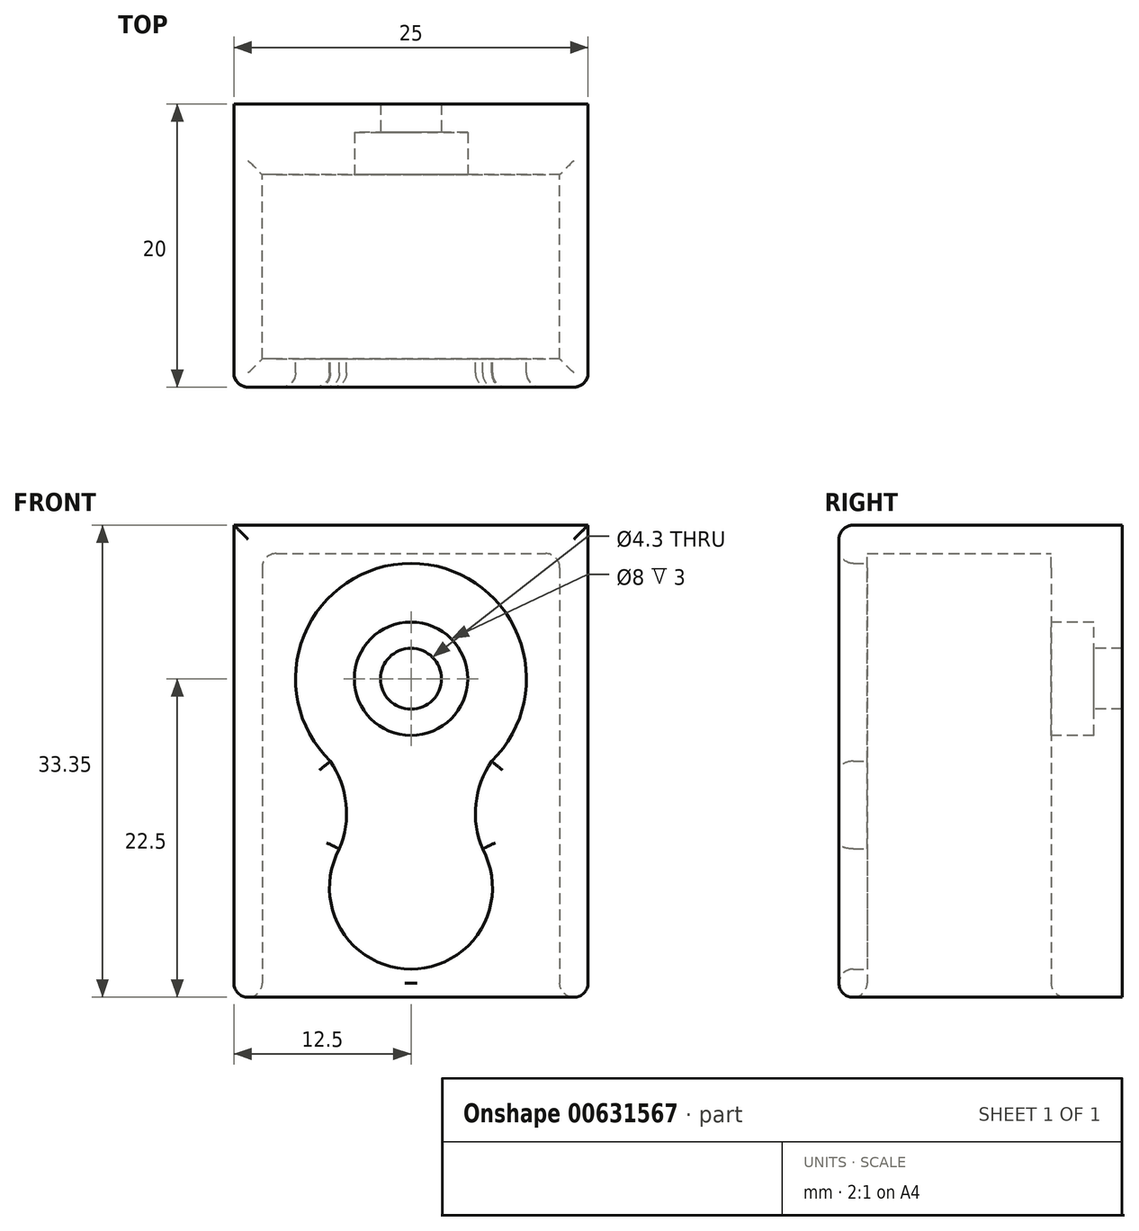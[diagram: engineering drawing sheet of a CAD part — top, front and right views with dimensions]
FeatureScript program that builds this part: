
annotation { "Feature Type Name" : "Feature", "Feature Type Description" : "" }
export const myFeature = defineFeature(function(context is Context, id is Id, definition is map)
    precondition{}
    {
        {
            var Q0;
            Q0=qCreatedBy(makeId("Front.planeOp"),FACE);
            var sketch = newSketch(context, id + "F0", { "sketchPlane" : qUnion([Q0])});
            skLineSegment(sketch, "E0.bottom", {"start": v(12.5, -22.5) * mm, "end": v(-12.5, -22.5) * mm});
            skLineSegment(sketch, "E0.top", {"start": v(12.5, 22.5) * mm, "end": v(-12.5, 22.5) * mm});
            skLineSegment(sketch, "E0.left", {"start": v(12.5, -22.5) * mm, "end": v(12.5, 22.5) * mm});
            skLineSegment(sketch, "E0.right", {"start": v(-12.5, -22.5) * mm, "end": v(-12.5, 22.5) * mm});
            skPoint(sketch, "E0.middle", {"position": v(0, 0) * mm});
            skCircle(sketch, "E1", {"center": v(0, 17.3) * mm, "radius": 2.15 * mm});
            skSolve(sketch);
        }
        {
            var Q0;
            Q0=makeQuery(id+"F0.imprint","IMPRINT",FACE,{"disambiguationData":[TD([[makeQuery(id+"F0.imprint","IMPRINT",EDGE,{"derivedFrom":sQuery(id+"F0.wireOp",EDGE,"E0.bottom")}),-1.0]])]});
            extrude(context, id + "F1", {"entities" : qUnion([Q0]), "depth" : 5 * mm, "offsetDistance" : 25 * mm});
        }
        {
            var Q0;
            Q0=makeQuery(id+"F1.opExtrude","CAP_FACE",FACE,{"disambiguationData":[OSD([sQuery(id+"F0.wireOp",EDGE,"E0.bottom"),sQuery(id+"F0.wireOp",EDGE,"E0.top"),sQuery(id+"F0.wireOp",EDGE,"E0.left"),sQuery(id+"F0.wireOp",EDGE,"E0.right"),sQuery(id+"F0.wireOp",EDGE,"E1")])],"isStart":false});
            var sketch = newSketch(context, id + "F2", { "sketchPlane" : qUnion([Q0])});
            skCircle(sketch, "E2", {"center": v(0, 17.3) * mm, "radius": 4 * mm});
            skSolve(sketch);
        }
        {
            var Q0;
            Q0 = qSketchRegion(id + "F2", true);
            extrude(context, id + "F3", {"entities" : qUnion([Q0]), "operationType" : NewBodyOperationType.REMOVE, "oppositeDirection" : true, "depth" : 3 * mm, "offsetDistance" : 25 * mm});
        }
        {
            var Q0;
            Q0=makeQuery(id+"F1.opExtrude","CAP_FACE",FACE,{"disambiguationData":[OSD([sQuery(id+"F0.wireOp",EDGE,"E0.bottom"),sQuery(id+"F0.wireOp",EDGE,"E0.top"),sQuery(id+"F0.wireOp",EDGE,"E0.left"),sQuery(id+"F0.wireOp",EDGE,"E0.right"),sQuery(id+"F0.wireOp",EDGE,"E1")])],"isStart":false});
            var sketch = newSketch(context, id + "F4", { "sketchPlane" : qUnion([Q0])});
            skLineSegment(sketch, "E3.bottom", {"start": v(-12.5, 10.85) * mm, "end": v(12.5, 10.85) * mm});
            skLineSegment(sketch, "E3.top", {"start": v(-12.5, -22.5) * mm, "end": v(-10.5, -22.5) * mm});
            skLineSegment(sketch, "E3.left", {"start": v(-12.5, 10.85) * mm, "end": v(-12.5, -22.5) * mm});
            skLineSegment(sketch, "E3.right", {"start": v(12.5, 10.85) * mm, "end": v(12.5, -22.5) * mm});
            skLineSegment(sketch, "E4.0", {"start": v(-10.5, 8.85) * mm, "end": v(10.5, 8.85) * mm});
            skLineSegment(sketch, "E4.1", {"start": v(-10.5, 8.85) * mm, "end": v(-10.5, -20.5) * mm});
            skLineSegment(sketch, "E4.3", {"start": v(10.5, 8.85) * mm, "end": v(10.5, -20.5) * mm});
            skLineSegment(sketch, "E5", {"start": v(10.5, -20.5) * mm, "end": v(10.5, -22.5) * mm});
            skLineSegment(sketch, "E6", {"start": v(-10.5, -20.5) * mm, "end": v(-10.5, -22.5) * mm});
            skLineSegment(sketch, "E7.trimOffspring", {"start": v(10.5, -22.5) * mm, "end": v(12.5, -22.5) * mm});
            skSolve(sketch);
        }
        {
            var Q0;
            Q0 = qSketchRegion(id + "F4", true);
            extrude(context, id + "F5", {"entities" : qUnion([Q0]), "operationType" : NewBodyOperationType.ADD, "depth" : 13 * mm, "offsetDistance" : 25 * mm});
        }
        {
            var Q0;
            Q0=makeQuery(id+"F5.opExtrude","CAP_FACE",FACE,{"disambiguationData":[OSD([sQuery(id+"F4.wireOp",EDGE,"E3.bottom"),sQuery(id+"F4.wireOp",EDGE,"E3.top"),sQuery(id+"F4.wireOp",EDGE,"E3.left"),sQuery(id+"F4.wireOp",EDGE,"E3.right"),sQuery(id+"F4.wireOp",EDGE,"E4.0"),sQuery(id+"F4.wireOp",EDGE,"E4.1"),sQuery(id+"F4.wireOp",EDGE,"E4.3"),sQuery(id+"F4.wireOp",EDGE,"E5"),sQuery(id+"F4.wireOp",EDGE,"E6"),sQuery(id+"F4.wireOp",EDGE,"E7.trimOffspring")])],"isStart":false});
            var sketch = newSketch(context, id + "F6", { "sketchPlane" : qUnion([Q0])});
            skLineSegment(sketch, "E8.0", {"start": v(-12.5, 10.85) * mm, "end": v(12.5, 10.85) * mm});
            skLineSegment(sketch, "E8.1", {"start": v(-12.5, -22.5) * mm, "end": v(-12.5, 10.85) * mm});
            skLineSegment(sketch, "E8.2", {"start": v(12.5, -22.5) * mm, "end": v(12.5, 10.85) * mm});
            skLineSegment(sketch, "E9", {"start": v(12.5, -22.5) * mm, "end": v(-12.5, -22.5) * mm});
            skArc(sketch, "E10", {"start": v(5.7, -5.83) * mm, "mid": v(0, 8.15) * mm, "end": v(-5.7, -5.83) * mm});
            skArc(sketch, "E11", {"start": v(-5.05, -12.02) * mm, "mid": v(0, -20.51) * mm, "end": v(5.05, -12.02) * mm});
            skArc(sketch, "E12", {"start": v(-5.32, -12.58) * mm, "mid": v(-4.56, -9.15) * mm, "end": v(-5.7, -5.83) * mm});
            skPoint(sketch, "E12.endSnap0", {"position": v(-12.5, -5.83) * mm});
            skLineSegment(sketch, "E13", {"start": v(0, 8.85) * mm, "end": v(0, -22.5) * mm, "construction": true});
            skArc(sketch, "E14.MirrorCS", {"start": v(5.32, -12.58) * mm, "mid": v(4.56, -9.15) * mm, "end": v(5.7, -5.83) * mm});
            skSolve(sketch);
        }
        {
            var Q0;
            {var subQ4=sQuery(id+"F6.wireOp",EDGE,"E10");Q0=makeQuery(id+"F6.imprint","IMPRINT",FACE,{"disambiguationData":[TD([[makeQuery(id+"F6.imprint","IMPRINT",EDGE,{"derivedFrom":subQ4}),-1.0]])]});}
            var Q1;
            Q1=makeQuery(id+"F6.imprint","IMPRINT",FACE,{"disambiguationData":[TD([[makeQuery(id+"F6.imprint","IMPRINT",EDGE,{"derivedFrom":sQuery(id+"F6.wireOp",EDGE,"E8.0")}),-1.0]])]});
            extrude(context, id + "F7", {"entities" : qUnion([Q0, Q1]), "operationType" : NewBodyOperationType.ADD, "depth" : 2 * mm, "offsetDistance" : 25 * mm});
        }
        {
            var Q0;
            {var subQ0=sQuery(id+"F0.wireOp",EDGE,"E0.right");var subQ1=sQuery(id+"F0.wireOp",EDGE,"E0.left");var subQ2=sQuery(id+"F0.wireOp",EDGE,"E0.top");Q0=makeQuery(id+"F5.boolean.opBoolean","SPLIT",FACE,{"disambiguationData":[TD([makeQuery(id+"F1.opExtrude","SWEPT_FACE",FACE,{"disambiguationData":[OSD([subQ2])]})])],"derivedFrom":makeQuery(id+"F1.opExtrude","CAP_FACE",FACE,{"disambiguationData":[OSD([sQuery(id+"F0.wireOp",EDGE,"E0.bottom"),subQ2,subQ1,subQ0,sQuery(id+"F0.wireOp",EDGE,"E1")])],"isStart":false})});}
            var sketch = newSketch(context, id + "F8", { "sketchPlane" : qUnion([Q0])});
            skLineSegment(sketch, "E15.0", {"start": v(12.5, 22.5) * mm, "end": v(-12.5, 22.5) * mm});
            skLineSegment(sketch, "E15.1", {"start": v(-12.5, 10.85) * mm, "end": v(-12.5, 22.5) * mm});
            skLineSegment(sketch, "E15.2", {"start": v(-12.5, 10.85) * mm, "end": v(12.5, 10.85) * mm});
            skLineSegment(sketch, "E15.3", {"start": v(12.5, 10.85) * mm, "end": v(12.5, 22.5) * mm});
            skSolve(sketch);
        }
        {
            var Q0;
            Q0 = qSketchRegion(id + "F8", true);
            var Q1;
            Q1=makeQuery(id+"F1.opExtrude","CAP_FACE",FACE,{"disambiguationData":[OSD([sQuery(id+"F0.wireOp",EDGE,"E0.bottom"),sQuery(id+"F0.wireOp",EDGE,"E0.top"),sQuery(id+"F0.wireOp",EDGE,"E0.left"),sQuery(id+"F0.wireOp",EDGE,"E0.right"),sQuery(id+"F0.wireOp",EDGE,"E1")])],"isStart":true});
            extrude(context, id + "F9", {"entities" : qUnion([Q0]), "operationType" : NewBodyOperationType.REMOVE, "endBound" : BoundingType.UP_TO_SURFACE, "oppositeDirection" : true, "depth" : 25 * mm, "endBoundEntityFace" : qUnion([Q1]), "offsetDistance" : 25 * mm});
        }
        {
            var Q0;
            {var subQ0=sQuery(id+"F0.wireOp",EDGE,"E0.bottom");Q0=makeQuery(id+"F5.boolean.opBoolean","SPLIT",FACE,{"disambiguationData":[TD([makeQuery(id+"F1.opExtrude","SWEPT_FACE",FACE,{"disambiguationData":[OSD([subQ0])]})])],"derivedFrom":makeQuery(id+"F1.opExtrude","CAP_FACE",FACE,{"disambiguationData":[OSD([subQ0,sQuery(id+"F0.wireOp",EDGE,"E0.top"),sQuery(id+"F0.wireOp",EDGE,"E0.left"),sQuery(id+"F0.wireOp",EDGE,"E0.right"),sQuery(id+"F0.wireOp",EDGE,"E1")])],"isStart":false})});}
            var sketch = newSketch(context, id + "F10", { "sketchPlane" : qUnion([Q0])});
            skCircle(sketch, "E16", {"center": v(0, 0) * mm, "radius": 2.15 * mm});
            skSolve(sketch);
        }
        {
            var Q0;
            Q0=makeQuery(id+"F10.imprint","IMPRINT",FACE,{"disambiguationData":[TD([[makeQuery(id+"F10.imprint","IMPRINT",EDGE,{"derivedFrom":sQuery(id+"F10.wireOp",EDGE,"E16")}),1.0]])]});
            extrude(context, id + "F11", {"entities" : qUnion([Q0]), "operationType" : NewBodyOperationType.REMOVE, "endBound" : BoundingType.UP_TO_NEXT, "oppositeDirection" : true, "depth" : 25 * mm, "offsetDistance" : 25 * mm});
        }
        {
            var Q0;
            {var subQ0=sQuery(id+"F0.wireOp",EDGE,"E0.bottom");Q0=makeQuery(id+"F5.boolean.opBoolean","SPLIT",FACE,{"disambiguationData":[TD([makeQuery(id+"F1.opExtrude","SWEPT_FACE",FACE,{"disambiguationData":[OSD([subQ0])]})])],"derivedFrom":makeQuery(id+"F1.opExtrude","CAP_FACE",FACE,{"disambiguationData":[OSD([subQ0,sQuery(id+"F0.wireOp",EDGE,"E0.top"),sQuery(id+"F0.wireOp",EDGE,"E0.left"),sQuery(id+"F0.wireOp",EDGE,"E0.right"),sQuery(id+"F0.wireOp",EDGE,"E1")])],"isStart":false})});}
            var sketch = newSketch(context, id + "F12", { "sketchPlane" : qUnion([Q0])});
            skCircle(sketch, "E17", {"center": v(0, 0) * mm, "radius": 4 * mm});
            skSolve(sketch);
        }
        {
            var Q0;
            Q0 = qSketchRegion(id + "F12", true);
            extrude(context, id + "F13", {"entities" : qUnion([Q0]), "operationType" : NewBodyOperationType.REMOVE, "oppositeDirection" : true, "depth" : 3 * mm, "offsetDistance" : 25 * mm});
        }
        {
            var Q0;
            Q0=makeQuery(id+"F7.opExtrude","CAP_EDGE",EDGE,{"disambiguationData":[OSD([sQuery(id+"F6.wireOp",EDGE,"E8.0")])],"isStart":false});
            var Q1;
            Q1=makeQuery(id+"F7.opExtrude","CAP_EDGE",EDGE,{"disambiguationData":[OSD([sQuery(id+"F6.wireOp",EDGE,"E8.1")])],"isStart":false});
            var Q2;
            Q2=makeQuery(id+"F7.opExtrude","CAP_EDGE",EDGE,{"disambiguationData":[OSD([sQuery(id+"F6.wireOp",EDGE,"E8.2")])],"isStart":false});
            var Q3;
            Q3=makeQuery(id+"F7.opExtrude","CAP_EDGE",EDGE,{"disambiguationData":[OSD([sQuery(id+"F6.wireOp",EDGE,"E9")])],"isStart":false});
            var Q4;
            Q4=makeQuery(id+"F9.boolean.opBoolean","MERGE",EDGE,{"derivedFrom":[makeQuery(id+"F7.boolean.opBoolean","MERGE",EDGE,{"derivedFrom":[makeQuery(id+"F5.opExtrude","SWEPT_EDGE",EDGE,{"disambiguationData":[OSD([sQuery(id+"F0.wireOp",EDGE,"E0.left"),sQuery(id+"F4.wireOp",EDGE,"E3.bottom"),sQuery(id+"F4.wireOp",EDGE,"E3.right")])]}),makeQuery(id+"F7.opExtrude","SWEPT_EDGE",EDGE,{"disambiguationData":[OSD([sQuery(id+"F6.wireOp",EDGE,"E8.0"),sQuery(id+"F6.wireOp",EDGE,"E8.2")])]})]}),makeQuery(id+"F9.opExtrude","SWEPT_EDGE",EDGE,{"disambiguationData":[OSD([sQuery(id+"F8.wireOp",EDGE,"E15.2"),sQuery(id+"F8.wireOp",EDGE,"E15.3")])]})]});
            var Q5;
            Q5=makeQuery(id+"F9.boolean.opBoolean","MERGE",EDGE,{"derivedFrom":[makeQuery(id+"F7.boolean.opBoolean","MERGE",EDGE,{"derivedFrom":[makeQuery(id+"F5.opExtrude","SWEPT_EDGE",EDGE,{"disambiguationData":[OSD([sQuery(id+"F0.wireOp",EDGE,"E0.right"),sQuery(id+"F4.wireOp",EDGE,"E3.bottom"),sQuery(id+"F4.wireOp",EDGE,"E3.left")])]}),makeQuery(id+"F7.opExtrude","SWEPT_EDGE",EDGE,{"disambiguationData":[OSD([sQuery(id+"F6.wireOp",EDGE,"E8.0"),sQuery(id+"F6.wireOp",EDGE,"E8.1")])]})]}),makeQuery(id+"F9.opExtrude","SWEPT_EDGE",EDGE,{"disambiguationData":[OSD([sQuery(id+"F8.wireOp",EDGE,"E15.1"),sQuery(id+"F8.wireOp",EDGE,"E15.2")])]})]});
            var Q6;
            Q6=makeQuery(id+"F7.boolean.opBoolean","MERGE",EDGE,{"derivedFrom":[makeQuery(id+"F5.boolean.opBoolean","MERGE",EDGE,{"derivedFrom":[makeQuery(id+"F1.opExtrude","SWEPT_EDGE",EDGE,{"disambiguationData":[OSD([sQuery(id+"F0.wireOp",EDGE,"E0.bottom"),sQuery(id+"F0.wireOp",EDGE,"E0.left")])]}),makeQuery(id+"F5.opExtrude","SWEPT_EDGE",EDGE,{"disambiguationData":[OSD([sQuery(id+"F4.wireOp",EDGE,"E3.right"),sQuery(id+"F4.wireOp",EDGE,"E7.trimOffspring")])]})]}),makeQuery(id+"F7.opExtrude","SWEPT_EDGE",EDGE,{"disambiguationData":[OSD([sQuery(id+"F6.wireOp",EDGE,"E8.2"),sQuery(id+"F6.wireOp",EDGE,"E9")])]})]});
            var Q7;
            Q7=makeQuery(id+"F7.boolean.opBoolean","MERGE",EDGE,{"derivedFrom":[makeQuery(id+"F5.boolean.opBoolean","MERGE",EDGE,{"derivedFrom":[makeQuery(id+"F1.opExtrude","SWEPT_EDGE",EDGE,{"disambiguationData":[OSD([sQuery(id+"F0.wireOp",EDGE,"E0.bottom"),sQuery(id+"F0.wireOp",EDGE,"E0.right")])]}),makeQuery(id+"F5.opExtrude","SWEPT_EDGE",EDGE,{"disambiguationData":[OSD([sQuery(id+"F4.wireOp",EDGE,"E3.top"),sQuery(id+"F4.wireOp",EDGE,"E3.left")])]})]}),makeQuery(id+"F7.opExtrude","SWEPT_EDGE",EDGE,{"disambiguationData":[OSD([sQuery(id+"F6.wireOp",EDGE,"E8.1"),sQuery(id+"F6.wireOp",EDGE,"E9")])]})]});
            var Q8;
            Q8=makeQuery(id+"F5.opExtrude","SWEPT_EDGE",EDGE,{"disambiguationData":[OSD([sQuery(id+"F0.wireOp",EDGE,"E0.bottom"),sQuery(id+"F4.wireOp",EDGE,"E5"),sQuery(id+"F4.wireOp",EDGE,"E7.trimOffspring")])]});
            var Q9;
            Q9=makeQuery(id+"F5.opExtrude","SWEPT_EDGE",EDGE,{"disambiguationData":[OSD([sQuery(id+"F0.wireOp",EDGE,"E0.bottom"),sQuery(id+"F4.wireOp",EDGE,"E3.top"),sQuery(id+"F4.wireOp",EDGE,"E6")])]});
            var Q10;
            Q10=makeQuery(id+"F7.opExtrude","CAP_EDGE",EDGE,{"disambiguationData":[OSD([sQuery(id+"F6.wireOp",EDGE,"E9")])],"isStart":true});
            var Q11;
            Q11=makeQuery(id+"F7.opExtrude","CAP_EDGE",EDGE,{"disambiguationData":[OSD([sQuery(id+"F6.wireOp",EDGE,"E10")])],"isStart":false});
            var Q12;
            Q12=makeQuery(id+"F7.opExtrude","CAP_EDGE",EDGE,{"disambiguationData":[OSD([sQuery(id+"F6.wireOp",EDGE,"E14.MirrorCS")])],"isStart":false});
            var Q13;
            Q13=makeQuery(id+"F7.opExtrude","CAP_EDGE",EDGE,{"disambiguationData":[OSD([sQuery(id+"F6.wireOp",EDGE,"E11")])],"isStart":false});
            var Q14;
            Q14=makeQuery(id+"F7.opExtrude","CAP_EDGE",EDGE,{"disambiguationData":[OSD([sQuery(id+"F6.wireOp",EDGE,"E12")])],"isStart":false});
            var Q15;
            Q15=makeQuery(id+"F1.opExtrude","CAP_EDGE",EDGE,{"disambiguationData":[OSD([sQuery(id+"F0.wireOp",EDGE,"E0.bottom")])],"isStart":false});
            var Q16;
            Q16=makeQuery(id+"F5.opExtrude","SWEPT_EDGE",EDGE,{"disambiguationData":[OSD([sQuery(id+"F4.wireOp",EDGE,"E4.0"),sQuery(id+"F4.wireOp",EDGE,"E4.1")])]});
            var Q17;
            Q17=makeQuery(id+"F5.opExtrude","SWEPT_EDGE",EDGE,{"disambiguationData":[OSD([sQuery(id+"F4.wireOp",EDGE,"E4.0"),sQuery(id+"F4.wireOp",EDGE,"E4.3")])]});
            var Q18;
            Q18=makeQuery(id+"F5.opExtrude","CAP_EDGE",EDGE,{"disambiguationData":[OSD([sQuery(id+"F4.wireOp",EDGE,"E4.1"),sQuery(id+"F4.wireOp",EDGE,"E6")])],"isStart":true});
            var Q19;
            Q19=makeQuery(id+"F5.opExtrude","CAP_EDGE",EDGE,{"disambiguationData":[OSD([sQuery(id+"F4.wireOp",EDGE,"E4.3"),sQuery(id+"F4.wireOp",EDGE,"E5")])],"isStart":true});
            fillet(context, id + "F14", {"entities" : qUnion([Q0, Q1, Q2, Q3, Q4, Q5, Q6, Q7, Q8, Q9, Q10, Q11, Q12, Q13, Q14, Q15, Q16, Q17, Q18, Q19]), "radius" : 1 * mm, "allowEdgeOverflow" : false});
        }
    });
